# Revit family: VIESSMANN - Vitocell 100-W CUG CUGA CUGA-A 100 L
name_source: partatom
category: Wyposażenie mechaniczne
revit_build: Autodesk Revit 2017 (Build: 20160720_1515(x64)
units: mm (PartAtom-declared; Revit-internal decimal feet)

## family parameters
Numer OmniClass = 23.65.35.11.11
Oparty na płaszczyźnie roboczej = Nie
Punkt obliczania pomieszczeń = Nie
Tnij formami wycięć po wczytaniu = Nie
Typ części = Normalny
Tytuł OmniClass = Storage Water Heaters
Współdzielony = Nie
Wymiar okrągłego złącza = Użyj średnicy
Zawsze pionowo = Tak

## types (1)
- Zbiornik CUG 100L
    Autor = https://www.archispace.pl
    Ciepła woda użytkowa = 3/4"
    Cyrkulacja = 3/4"
    Dop. ciśnienie robocze po stronie wody grzewczej = 1000.000 kPa
    Dop. ciśnienie robocze po stronie wody użytkowej = 1000.000 kPa
    Dop. temperatura po stronie cwu = 95 °C
    Dop. temperatura po stronie wody grzewczej = 160 °C
    Długość = 574 mm  [stored 1.8832 ft]
    Ilość ciepła dyżurnego = 1.49 kWh/24h
    Klasa efektywności energetycznej = C
    Masa całkowita = 51.00 kg
    Model = Podgrzewacz pojemnościowy Viessmann Vitocell 100-W CUG 100L / Hot water storage tank Viessmann Vitocell 100-W CUG 100L
    Numer identyfikacyjny produktu = 9W245/11-13MC/E
    Opis = Pojemnościowy podgrzewacz wody
    Opis indeksowy = 9W245/11-13MC/E
    Pojemność podgrzewacza = 100.0 L
    Powierzchnia grzewcza = 0.9 cm²
    Powrót wody grzewczej = 1"
    Producent = Viessmann Sp.z.o.o.
    URL = https://www.viessmann-projektant.pl
    Viessmann Kolor 1 = Viessmann Kolor 1
    Viessmann Kolor 2 = Viessmann Kolor 2
    Viessmann Kolor 3 = Viessmann Kolor 3
    Wysokość = 836 mm  [stored 2.74278 ft]
    Zasilanie wody grzewczej = 1"
    Zimna woda użytkowa = 3/4"
    Średnica = 553 mm  [stored 1.8143 ft]

note: [stored X ft] marks values corroborated as IEEE doubles in the binary element streams (Revit-internal decimal feet)
